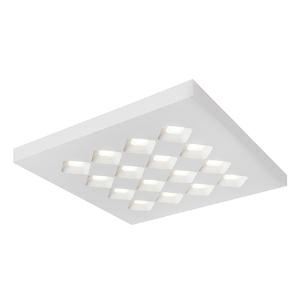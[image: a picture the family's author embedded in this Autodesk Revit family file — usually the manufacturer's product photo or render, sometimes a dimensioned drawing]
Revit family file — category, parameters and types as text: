
# Revit family: 3f_filippi_-_3f_diagon_p_soft_ugr_3f_filippi_-_12136_-_3f_diagon_p_39w-930_ep_soft_ugr_596x596
name_source: partatom
category: Lighting Fixtures
units: mm (PartAtom-declared; Revit-internal decimal feet)

## family parameters
Cut with Voids When Loaded = No
Host = Face
Light Source = No
Part Type = Normal
Room Calculation Point = No
Round Connector Dimension = Use Diameter
Shared = No

## types (1)
- 3F Filippi - 3F Dìagon P Soft UGR (1 x LED, 3664 lm, 41 W, 3000 K)
    Apparent Load = 41 VA
    Approval mark = ENEC
    CIE Flux Codes = 59 92 100 100 100
    Color Rendering = 90
    Color Temperature = 3000 K
    Control Gear = Electronic ballast
    Default Elevation = 1800 mm
    Description = ILLUMINOTECHNICAL
Luminous efficiency 100% (DLOR 100%, ULOR 0%).
Initial luminous flux of the luminaire 3664 lm.
Emergency luminaire luminous flux BLF 13%.
Direct symmetric distribution.
Installation Interdistance Transv.D = 1.23 x hu - Long.D = 1.23 x hu.
Average luminance <3000 cd/m² for radial angles >65°.
Tabular UGR (CIE 117 - 4H-8H; S=0.25H; 70/50/20): RUG 18.7 - 18.7.
Beam angle: 102° - 101°.
Luminous efficacy 89 lm/W.
Lifetime (L90/B10): 30000 h. (tq+25°C)
Lifetime (L85/B10): 50000 h. (tq+25°C)
Lifetime (L80/B20): 80000 h. (tq+25°C)
Lifetime (L70/B20): 100000 h. (tq+25°C)
Sudden decreased luminous flux after 50000 hours: 0% (C0).
Photobiological safety in compliance with IEC/TR 62778: RG0 risk exempt, (IEC 62471).
In compliance with IEC/EN 62722-2-1 - IEC/EN 62717 standards.

SOURCE
Squared LED module 39W/930.
Energy efficiency class (UE 2019/2020 - UE 2019/2015): E.
CIE 13.3 Colour rendering index: CRI >90 (R9 >50%).
IES TM-30 Fidelity Index: Rf = 92 Rg = 101.
CCT nominal colour temperature 3000 K.
Colour initial tolerance (MacAdam): SDCM 3.

MECHANICAL
White painted frame.
Height only 40 mm.
Housing in hot-galvanised steel, painted in white polyester.
Honeycombed diagonal screen in white anti-glare polycarbonate.
Opal methacrylate (PMMA) rhomboid lenses with differentiated, engraved and prismatic surfaces for diffused, soft lighting and excellent visual comfort.
Luminaire with limited surface temperature. - D - (EN 60598-2-24)
Dimensions: 596x596 mm, height 40 mm. Weight 7.095 kg.
IP40 protection degree.
Mechanical strength to impacts IK06 (1 joule).
Glow-wire test resistance 650°C.

ELECTRICAL
Halogen Free electronic wiring 230V-50/60Hz, power factor 0.90, THD <25%, constant output current, class I, 1 driver.
Power of the luminaire 41 W.
CE - IEC 60598-1 - EN 60598-1.
EP maintained emergency wiring on board, 1h duration, 24h recharge; compliant with EN 60598-2-22, excluding high risk areas.
SAFE FLICKER: PstLM=<1 and SVM=<0.4 (IEC TR 61547-1 and IEC TR 63158), to ensure a more comfortable and safe light.
Ambient temperature from +5°C to +25°C.
Temperature class T6 max 85°C.
Quick connection.
Relative humidity UR: <85%.

INSTALLATION
Ceiling.

APPLICATIONS
Environments: staterooms, with VDTs, offices.
Environments with exacting visual tasks, where diffused soft light for optimum visual comfort is required.

WARNING
Luminaire designed for disposal/recycling at end-of-life.
Replaceable (LED only) light source by a professional. Replaceable control gear by a professional.
    Height = 40 mm  [stored 0.131234 ft]
    Lamp = 1 x LED
    Lamp Light Flux = 3664 lm
    Lamp Power = 41 W
    Lamp count = 1
    Length = 596 mm
    Lifetime = 50000 h
    Luminous efficacy = 89 lm/W
    Manufacturer = 3F Filippi
    ModVariant = No
    Model = 3F Filippi - 12136 - 3F Diagon P 39W-930 EP SOFT UGR 596x596
    Mounting Place = Ceiling
    Mounting Type = Surface mounted
    Number of Poles = 1
    OnlyDefault = Yes
    Power Factor = 1
    Product Name = 3F Filippi - 3F Dìagon P Soft UGR
    Product group = ceiling mounted luminaire
    ProductGroupID = 3
    Protection Class = Protection class I
    Protection Degree = IP 40
    RLX_Detail_Level = 1
    RLX_Emergency_Light_Flux = 0 lm
    RLX_Emergency_Type = 0
    RLX_Emergency_Type_DB = No
    RlxData = <blob elided: 94877 chars, md5=0d813c2c>
    Socket = socket
    Standby Power = 0 W
    System Light Flux = 3664 lm
    System Power = 41 W
    Type Comments = Product without accessories
    Type Image = 3ffilippi_3f_diagon_p_soft_ugr.jpg
    URL = http://relux.com
    VarID = ---
    Voltage = 0 V
    Weight = 0.00 kg
    Width = 596 mm

note: [stored X ft] marks values corroborated as IEEE doubles in the binary element streams (Revit-internal decimal feet)

## geometry (parser evidence)
native form markers: Blend x4, Sweep x9
no freeform markers — native parametric forms only
